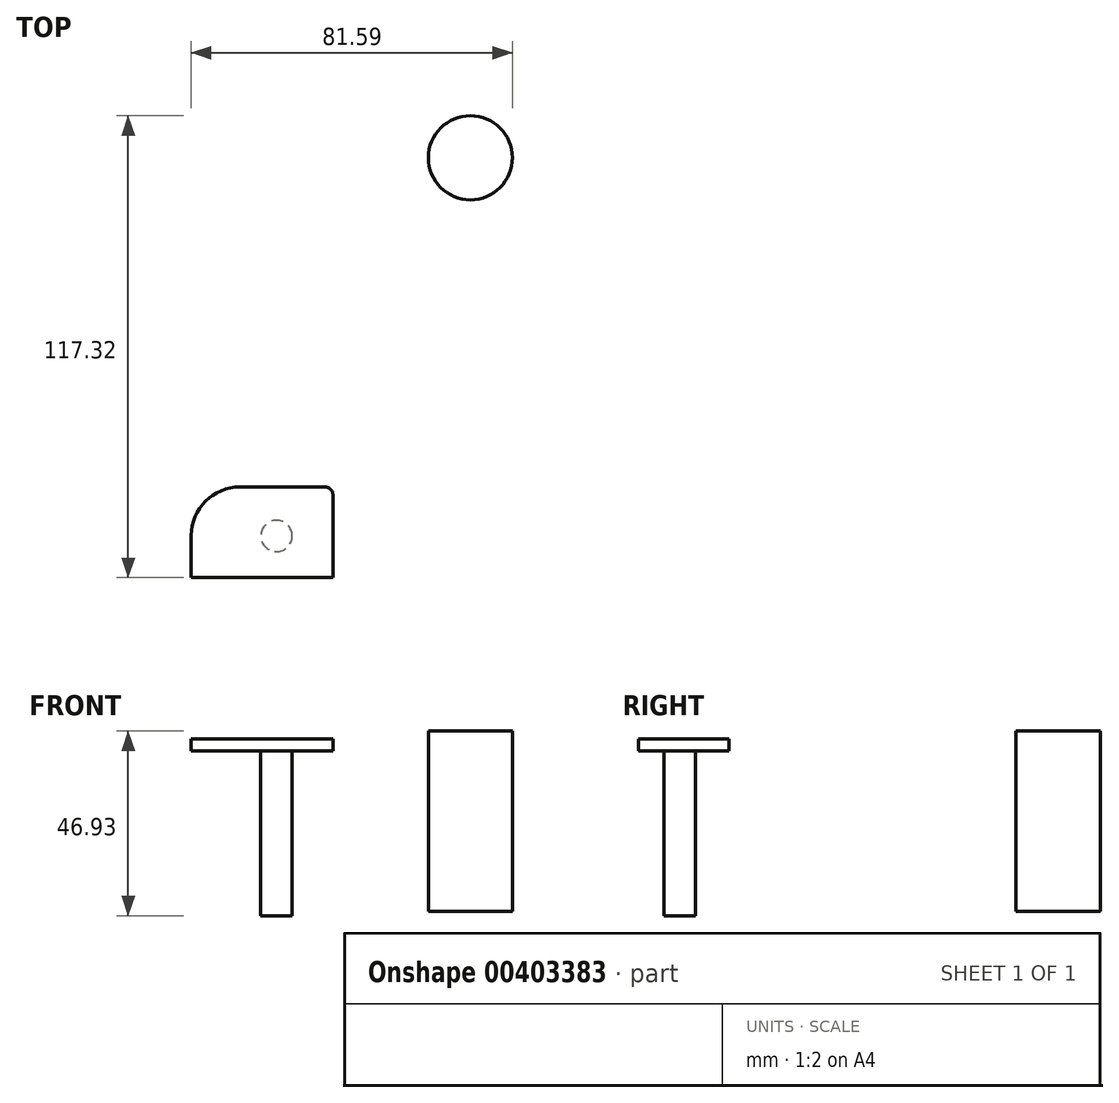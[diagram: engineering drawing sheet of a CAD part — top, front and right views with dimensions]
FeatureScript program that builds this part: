
annotation { "Feature Type Name" : "Feature", "Feature Type Description" : "" }
export const myFeature = defineFeature(function(context is Context, id is Id, definition is map)
    precondition{}
    {
        {
            var Q0;
            Q0=qCreatedBy(makeId("Top.planeOp"),FACE);
            var sketch = newSketch(context, id + "F0", { "sketchPlane" : qUnion([Q0])});
            skLineSegment(sketch, "E0", {"start": v(76.55, -12.69) * mm, "end": v(26.8, 40.74) * mm});
            skLineSegment(sketch, "E1.bottom", {"start": v(-23.28, -15.16) * mm, "end": v(-49.94, -15.16) * mm});
            skLineSegment(sketch, "E1.top", {"start": v(-23.28, -42.63) * mm, "end": v(-49.94, -42.63) * mm});
            skLineSegment(sketch, "E1.left", {"start": v(-23.28, -15.16) * mm, "end": v(-23.28, -42.63) * mm});
            skLineSegment(sketch, "E1.right", {"start": v(-49.94, -15.16) * mm, "end": v(-49.94, -42.63) * mm});
            skLineSegment(sketch, "E2.bottom", {"start": v(-13.67, 50.75) * mm, "end": v(-48.31, 50.75) * mm});
            skLineSegment(sketch, "E2.top", {"start": v(-13.67, 19.08) * mm, "end": v(-48.31, 19.08) * mm});
            skLineSegment(sketch, "E2.left", {"start": v(-13.67, 50.75) * mm, "end": v(-13.67, 19.08) * mm});
            skLineSegment(sketch, "E2.right", {"start": v(-48.31, 50.75) * mm, "end": v(-48.31, 19.08) * mm});
            skPoint(sketch, "E2.middle", {"position": v(-31, 34.92) * mm});
            skCircle(sketch, "E3", {"center": v(18.27, 62.25) * mm, "radius": 10.68 * mm});
            skSolve(sketch);
        }
        {
            var Q0;
            Q0=makeQuery(id+"F0.imprint","IMPRINT",FACE,{"disambiguationData":[TD([[makeQuery(id+"F0.imprint","IMPRINT",EDGE,{"derivedFrom":sQuery(id+"F0.wireOp",EDGE,"E3")}),1.0]])]});
            extrude(context, id + "F1", {"entities" : qUnion([Q0]), "depth" : 5 * mm});
        }
        {
            var Q0;
            Q0=qCreatedBy(makeId("Top.planeOp"),FACE);
            var sketch = newSketch(context, id + "F2", { "sketchPlane" : qUnion([Q0])});
            skLineSegment(sketch, "E4.bottom", {"start": v(-18.65, -21.38) * mm, "end": v(-52.64, -21.38) * mm});
            skLineSegment(sketch, "E4.top", {"start": v(-16.65, -44.39) * mm, "end": v(-52.64, -44.39) * mm});
            skLineSegment(sketch, "E4.left", {"start": v(-16.65, -23.38) * mm, "end": v(-16.65, -44.39) * mm});
            skLineSegment(sketch, "E4.right", {"start": v(-52.64, -21.38) * mm, "end": v(-52.64, -44.39) * mm});
            skPoint(sketch, "E4.middle", {"position": v(-34.65, -32.89) * mm});
            skPoint(sketch, "E5.visualSharp", {"position": v(-16.65, -21.38) * mm});
            skArc(sketch, "E5.filletArc", {"start": v(-16.65, -23.38) * mm, "mid": v(-17.23, -21.97) * mm, "end": v(-18.65, -21.38) * mm});
            skSolve(sketch);
        }
        {
            var Q0;
            Q0 = qSketchRegion(id + "F2", true);
            extrude(context, id + "F3", {"entities" : qUnion([Q0]), "depth" : 3 * mm});
        }
        {
            var Q0;
            Q0=makeQuery(id+"F3.opExtrude","SWEPT_EDGE",EDGE,{"disambiguationData":[OSD([sQuery(id+"F2.wireOp",EDGE,"E4.bottom"),sQuery(id+"F2.wireOp",EDGE,"E4.right")])]});
            fillet(context, id + "F4", {"entities" : qUnion([Q0]), "radius" : 12.35 * mm, "tangentPropagation" : true, "allowEdgeOverflow" : false});
        }
        {
            var Q0;
            Q0=makeQuery(id+"F3.opExtrude","CAP_FACE",FACE,{"disambiguationData":[OSD([sQuery(id+"F2.wireOp",EDGE,"E4.bottom"),sQuery(id+"F2.wireOp",EDGE,"E4.top"),sQuery(id+"F2.wireOp",EDGE,"E4.left"),sQuery(id+"F2.wireOp",EDGE,"E4.right"),sQuery(id+"F2.wireOp",EDGE,"E5.filletArc")])],"isStart":false});
            var sketch = newSketch(context, id + "F5", { "sketchPlane" : qUnion([Q0])});
            skCircle(sketch, "E6", {"center": v(-31, -33.83) * mm, "radius": 4 * mm});
            skSolve(sketch);
        }
        {
            var Q0;
            Q0=makeQuery(id+"F5.imprint","IMPRINT",FACE,{"disambiguationData":[TD([[makeQuery(id+"F5.imprint","IMPRINT",EDGE,{"derivedFrom":sQuery(id+"F5.wireOp",EDGE,"E6")}),1.0]])]});
            extrude(context, id + "F6", {"entities" : qUnion([Q0]), "operationType" : NewBodyOperationType.ADD, "oppositeDirection" : true, "depth" : 44.93 * mm});
        }
        {
            var Q0;
            Q0=makeQuery(id+"F1.opExtrude","CAP_FACE",FACE,{"disambiguationData":[OSD([sQuery(id+"F0.wireOp",EDGE,"E3")])],"isStart":true});
            extrude(context, id + "F7", {"entities" : qUnion([Q0]), "operationType" : NewBodyOperationType.ADD, "depth" : 40.86 * mm, "offsetDistance" : 25.4 * mm});
        }
    });
